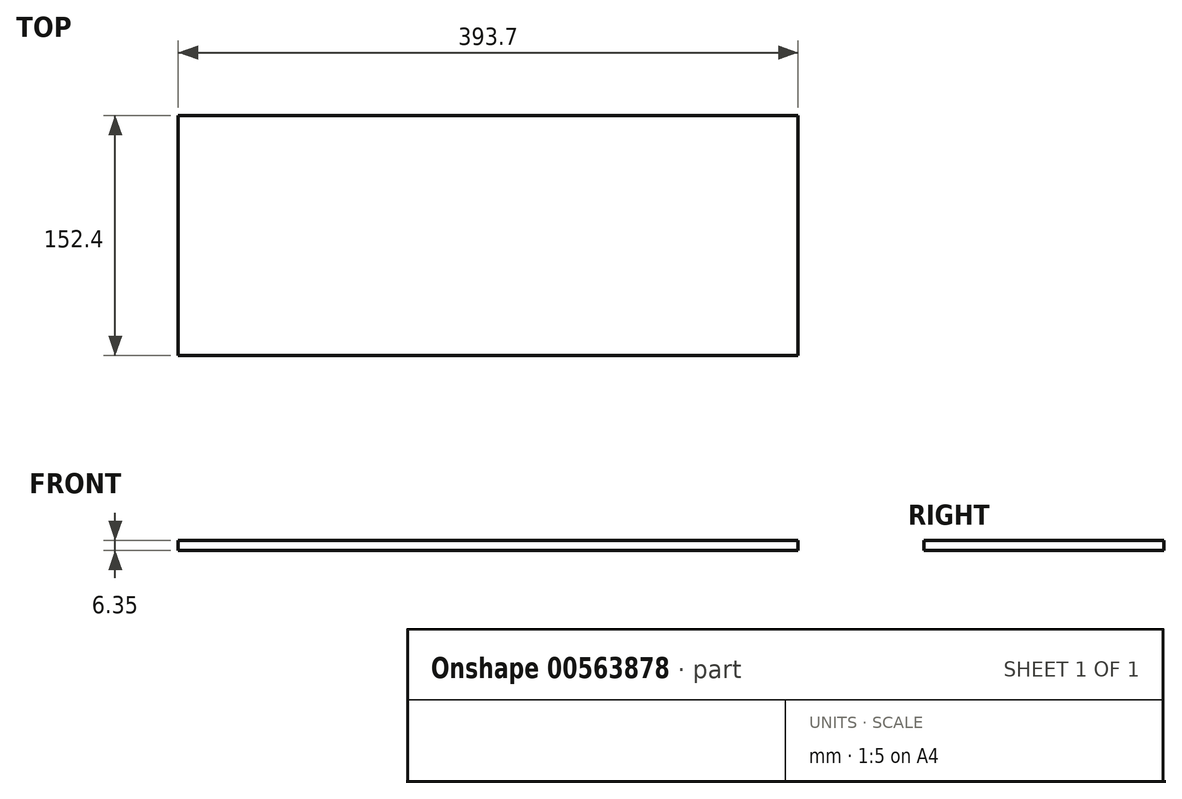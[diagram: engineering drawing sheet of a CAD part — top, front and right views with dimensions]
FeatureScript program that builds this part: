
annotation { "Feature Type Name" : "Feature", "Feature Type Description" : "" }
export const myFeature = defineFeature(function(context is Context, id is Id, definition is map)
    precondition{}
    {
        {
            var Q0;
            Q0=qCreatedBy(makeId("Top.planeOp"),FACE);
            var sketch = newSketch(context, id + "F0", { "sketchPlane" : qUnion([Q0])});
            skLineSegment(sketch, "E0.bottom", {"start": v(0, 0) * mm, "end": v(393.7, 0) * mm});
            skLineSegment(sketch, "E0.top", {"start": v(0, 152.4) * mm, "end": v(393.7, 152.4) * mm});
            skLineSegment(sketch, "E0.left", {"start": v(0, 0) * mm, "end": v(0, 152.4) * mm});
            skLineSegment(sketch, "E0.right", {"start": v(393.7, 0) * mm, "end": v(393.7, 152.4) * mm});
            skSolve(sketch);
        }
        {
            var Q0;
            Q0 = qSketchRegion(id + "F0", true);
            extrude(context, id + "F1", {"entities" : qUnion([Q0]), "depth" : 6.35 * mm, "offsetDistance" : 25.4 * mm});
        }
    });
